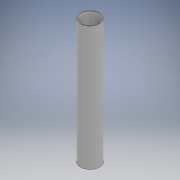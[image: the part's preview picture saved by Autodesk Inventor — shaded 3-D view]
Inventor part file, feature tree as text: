
AUTODESK INVENTOR PART (.ipt)
format: ipt  version: 2017 (Build 210142000, 142)  size: 94,208 bytes
history: native  units: mm
features: extrude x1, sketch x1
ambient origin geometry x8: Origin, YZ Plane, XZ Plane, XY Plane, X Axis, Y Axis, Z Axis, Center Point
bodies: Body1 (feature_tree)
feature tree (2):
  extrude  "Extrusion2"  Depth=500.0mm
  sketch  "Sketch1"  dims[d0=77.0mm d3=2.0mm d4=500.0mm d5=0.0mm]
